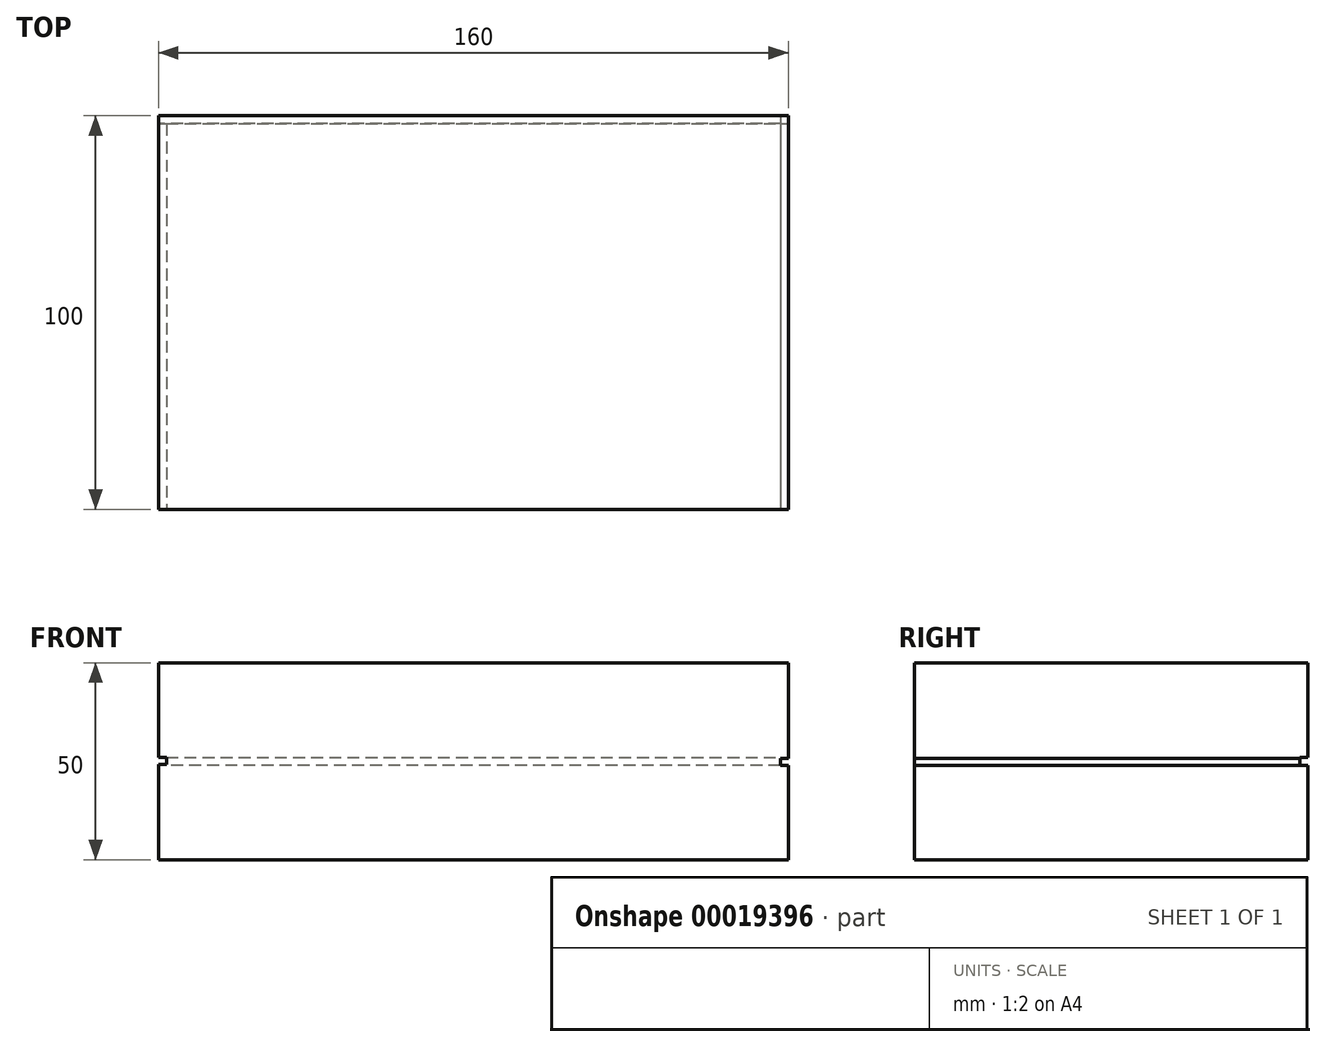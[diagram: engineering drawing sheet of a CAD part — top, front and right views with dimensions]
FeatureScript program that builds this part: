
annotation { "Feature Type Name" : "Feature", "Feature Type Description" : "" }
export const myFeature = defineFeature(function(context is Context, id is Id, definition is map)
    precondition{}
    {
        {
            var Q0;
            Q0=qCreatedBy(makeId("Top.planeOp"),FACE);
            var sketch = newSketch(context, id + "F0", { "sketchPlane" : qUnion([Q0])});
            skLineSegment(sketch, "E0.bottom", {"start": v(-79.06, -60.04) * mm, "end": v(80.94, -60.04) * mm});
            skLineSegment(sketch, "E0.top", {"start": v(-79.06, 39.96) * mm, "end": v(80.94, 39.96) * mm});
            skLineSegment(sketch, "E0.left", {"start": v(-79.06, -60.04) * mm, "end": v(-79.06, 39.96) * mm});
            skLineSegment(sketch, "E0.right", {"start": v(80.94, -60.04) * mm, "end": v(80.94, 39.96) * mm});
            skSolve(sketch);
        }
        {
            var Q0;
            Q0 = qSketchRegion(id + "F0", true);
            extrude(context, id + "F1", {"entities" : qUnion([Q0]), "depth" : 50 * mm});
        }
        {
            var Q0;
            Q0=makeQuery(id+"F1.opExtrude","SWEPT_FACE",FACE,{"disambiguationData":[OSD([sQuery(id+"F0.wireOp",EDGE,"E0.top")])]});
            var sketch = newSketch(context, id + "F2", { "sketchPlane" : qUnion([Q0])});
            skLineSegment(sketch, "E1", {"start": v(79.06, 25) * mm, "end": v(-80.94, 25) * mm});
            skLineSegment(sketch, "E2", {"start": v(-80.94, 25) * mm, "end": v(-80.94, 24) * mm});
            skLineSegment(sketch, "E3", {"start": v(-80.94, 24) * mm, "end": v(79.06, 24) * mm});
            skLineSegment(sketch, "E4", {"start": v(79.06, 24) * mm, "end": v(79.06, 25) * mm});
            skLineSegment(sketch, "E5", {"start": v(79.06, 25) * mm, "end": v(79.06, 26) * mm});
            skLineSegment(sketch, "E6", {"start": v(79.06, 26) * mm, "end": v(-80.94, 26) * mm});
            skLineSegment(sketch, "E7", {"start": v(-80.94, 26) * mm, "end": v(-80.94, 25) * mm});
            skSolve(sketch);
        }
        {
            var Q0;
            Q0=makeQuery(id+"F1.opExtrude","SWEPT_FACE",FACE,{"disambiguationData":[OSD([sQuery(id+"F0.wireOp",EDGE,"E0.left")])]});
            var sketch = newSketch(context, id + "F3", { "sketchPlane" : qUnion([Q0])});
            skLineSegment(sketch, "E8", {"start": v(-39.96, 25) * mm, "end": v(60.04, 25) * mm});
            skLineSegment(sketch, "E9", {"start": v(60.04, 25) * mm, "end": v(60.04, 24.23) * mm});
            skLineSegment(sketch, "E10", {"start": v(60.04, 24.23) * mm, "end": v(-39.96, 24.23) * mm});
            skLineSegment(sketch, "E11", {"start": v(-39.96, 24.23) * mm, "end": v(-39.96, 25) * mm});
            skLineSegment(sketch, "E12", {"start": v(-39.96, 25) * mm, "end": v(-39.96, 26) * mm});
            skLineSegment(sketch, "E13", {"start": v(-39.96, 26) * mm, "end": v(60.04, 26) * mm});
            skLineSegment(sketch, "E14", {"start": v(60.04, 26) * mm, "end": v(60.04, 25) * mm});
            skSolve(sketch);
        }
        {
            var Q0;
            Q0=makeQuery(id+"F1.opExtrude","SWEPT_FACE",FACE,{"disambiguationData":[OSD([sQuery(id+"F0.wireOp",EDGE,"E0.right")])]});
            var sketch = newSketch(context, id + "F4", { "sketchPlane" : qUnion([Q0])});
            skLineSegment(sketch, "E15.bottom", {"start": v(39.96, 23.96) * mm, "end": v(-60.04, 23.96) * mm});
            skLineSegment(sketch, "E15.top", {"start": v(39.96, 25.7) * mm, "end": v(-60.04, 25.7) * mm});
            skLineSegment(sketch, "E15.left", {"start": v(39.96, 23.96) * mm, "end": v(39.96, 25.7) * mm});
            skLineSegment(sketch, "E15.right", {"start": v(-60.04, 23.96) * mm, "end": v(-60.04, 25.7) * mm});
            skSolve(sketch);
        }
        {
            var Q0;
            Q0 = qSketchRegion(id + "F2", true);
            extrude(context, id + "F5", {"entities" : qUnion([Q0]), "operationType" : NewBodyOperationType.REMOVE, "oppositeDirection" : true, "depth" : 2 * mm});
        }
        {
            var Q0;
            Q0 = qSketchRegion(id + "F3", true);
            extrude(context, id + "F6", {"entities" : qUnion([Q0]), "operationType" : NewBodyOperationType.REMOVE, "oppositeDirection" : true, "depth" : 2 * mm});
        }
        {
            var Q0;
            Q0 = qSketchRegion(id + "F4", true);
            extrude(context, id + "F7", {"entities" : qUnion([Q0]), "operationType" : NewBodyOperationType.REMOVE, "oppositeDirection" : true, "depth" : 2 * mm});
        }
    });
